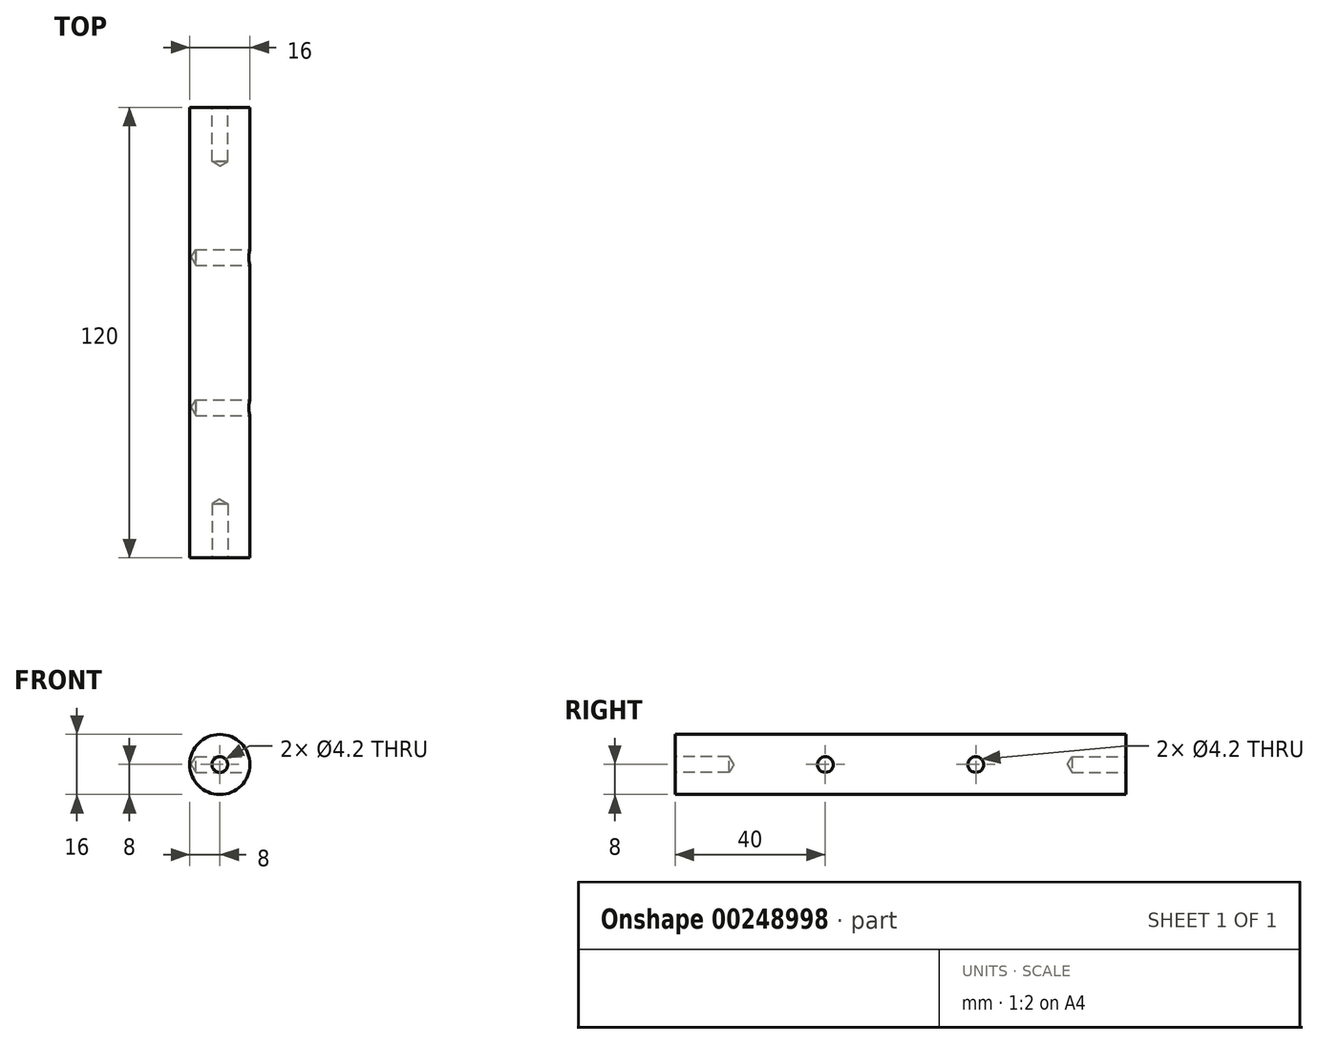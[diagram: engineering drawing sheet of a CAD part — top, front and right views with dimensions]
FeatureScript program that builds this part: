
annotation { "Feature Type Name" : "Feature", "Feature Type Description" : "" }
export const myFeature = defineFeature(function(context is Context, id is Id, definition is map)
    precondition{}
    {
        {
            var Q0;
            Q0=qCreatedBy(makeId("Front.planeOp"),FACE);
            var sketch = newSketch(context, id + "F0", { "sketchPlane" : qUnion([Q0])});
            skCircle(sketch, "E0", {"center": v(0, 0) * mm, "radius": 8 * mm});
            skSolve(sketch);
        }
        {
            var Q0;
            Q0=makeQuery(id+"F0.imprint","IMPRINT",FACE,{"disambiguationData":[TD([[makeQuery(id+"F0.imprint","IMPRINT",EDGE,{"derivedFrom":sQuery(id+"F0.wireOp",EDGE,"E0")}),1.0]])]});
            extrude(context, id + "F1", {"entities" : qUnion([Q0]), "endBound" : BoundingType.SYMMETRIC, "depth" : 120 * mm});
        }
        {
            var Q0;
            Q0=makeQuery(id+"F1.opExtrude","CAP_FACE",FACE,{"disambiguationData":[OSD([sQuery(id+"F0.wireOp",EDGE,"E0")])],"isStart":false});
            var sketch = newSketch(context, id + "F2", { "sketchPlane" : qUnion([Q0])});
            skPoint(sketch, "E1.0", {"position": v(0, 0) * mm});
            skSolve(sketch);
        }
        {
            var Q0;
            Q0=sQuery(id+"F2.wireOp",VERTEX,"E1.0");
            var Q1;
            Q1=makeQuery(id+"F1.opExtrude","SWEPT_BODY",BODY,{"disambiguationData":[OSD([sQuery(id+"F0.wireOp",EDGE,"E0")])]});
            hole(context, id + "F3", {"style" : HoleStyle.SIMPLE, "endStyle" : HoleEndStyle.BLIND, "standardTappedOrClearance" : lookupTablePath({ "standard" : "ISO", "engagement" : "75%", "pitch" : "0.8 mm", "size" : "M5", "type" : "Tapped" }), "standardBlindInLast" : lookupTablePath({ "standard" : "ISO", "engagement" : "75%", "pitch" : "0.8 mm", "size" : "M5", "type" : "Tapped" }), "holeDiameter" : 4.2 * mm, "showTappedDepth" : true, "holeDepth" : 14.4 * mm, "tappedDepth" : 12 * mm, "tapClearance" : 3, "startFromSketch" : true, "locations" : qUnion([Q0]), "scope" : qUnion([Q1]), "majorDiameter" : 5 * mm});
        }
        {
            var Q0;
            Q0=makeQuery(id+"F1.opExtrude","CAP_FACE",FACE,{"disambiguationData":[OSD([sQuery(id+"F0.wireOp",EDGE,"E0")])],"isStart":true});
            var sketch = newSketch(context, id + "F4", { "sketchPlane" : qUnion([Q0])});
            skPoint(sketch, "E2.0", {"position": v(0, 0) * mm});
            skSolve(sketch);
        }
        {
            var Q0;
            Q0=sQuery(id+"F4.wireOp",VERTEX,"E2.0");
            var Q1;
            Q1=makeQuery(id+"F1.opExtrude","SWEPT_BODY",BODY,{"disambiguationData":[OSD([sQuery(id+"F0.wireOp",EDGE,"E0")])]});
            hole(context, id + "F5", {"style" : HoleStyle.SIMPLE, "endStyle" : HoleEndStyle.BLIND, "standardTappedOrClearance" : lookupTablePath({ "standard" : "ISO", "engagement" : "75%", "pitch" : "0.8 mm", "size" : "M5", "type" : "Tapped" }), "standardBlindInLast" : lookupTablePath({ "standard" : "ISO", "engagement" : "75%", "pitch" : "0.8 mm", "size" : "M5", "type" : "Tapped" }), "holeDiameter" : 4.2 * mm, "showTappedDepth" : true, "holeDepth" : 14.4 * mm, "tappedDepth" : 12 * mm, "tapClearance" : 3, "startFromSketch" : true, "locations" : qUnion([Q0]), "scope" : qUnion([Q1]), "majorDiameter" : 5 * mm});
        }
        {
            var Q0;
            Q0=qCreatedBy(makeId("Right.planeOp"),FACE);
            var Q1;
            Q1=qBodyType(qCreatedBy(id+"Fvoa7d1aX5LAHPi_1",EDGE),BodyType.WIRE);
            cPlane(context, id + "F6", {"entities" : qUnion([Q0, Q1]), "cplaneType" : CPlaneType.OFFSET, "offset" : 8 * mm, "width" : 150 * mm, "height" : 150 * mm});
        }
        {
            var Q0;
            Q0=qCreatedBy(id+"F6.planeOp",FACE);
            var sketch = newSketch(context, id + "F7", { "sketchPlane" : qUnion([Q0])});
            skPoint(sketch, "E3", {"position": v(20, 0) * mm});
            skPoint(sketch, "E4", {"position": v(-20, 0) * mm});
            skSolve(sketch);
        }
        {
            var Q0;
            Q0=sQuery(id+"F7.wireOp",VERTEX,"E3");
            var Q1;
            Q1=sQuery(id+"F7.wireOp",VERTEX,"E4");
            var Q2;
            Q2=makeQuery(id+"F1.opExtrude","SWEPT_BODY",BODY,{"disambiguationData":[OSD([sQuery(id+"F0.wireOp",EDGE,"E0")])]});
            hole(context, id + "F8", {"style" : HoleStyle.SIMPLE, "endStyle" : HoleEndStyle.BLIND, "standardTappedOrClearance" : lookupTablePath({ "standard" : "ISO", "engagement" : "75%", "pitch" : "0.8 mm", "size" : "M5", "type" : "Tapped" }), "standardBlindInLast" : lookupTablePath({ "standard" : "ISO", "engagement" : "75%", "pitch" : "0.8 mm", "size" : "M5", "type" : "Tapped" }), "holeDiameter" : 4.2 * mm, "showTappedDepth" : true, "holeDepth" : 14.4 * mm, "tappedDepth" : 12 * mm, "tapClearance" : 3, "startFromSketch" : true, "locations" : qUnion([Q0, Q1]), "scope" : qUnion([Q2]), "majorDiameter" : 5 * mm});
        }
    });
